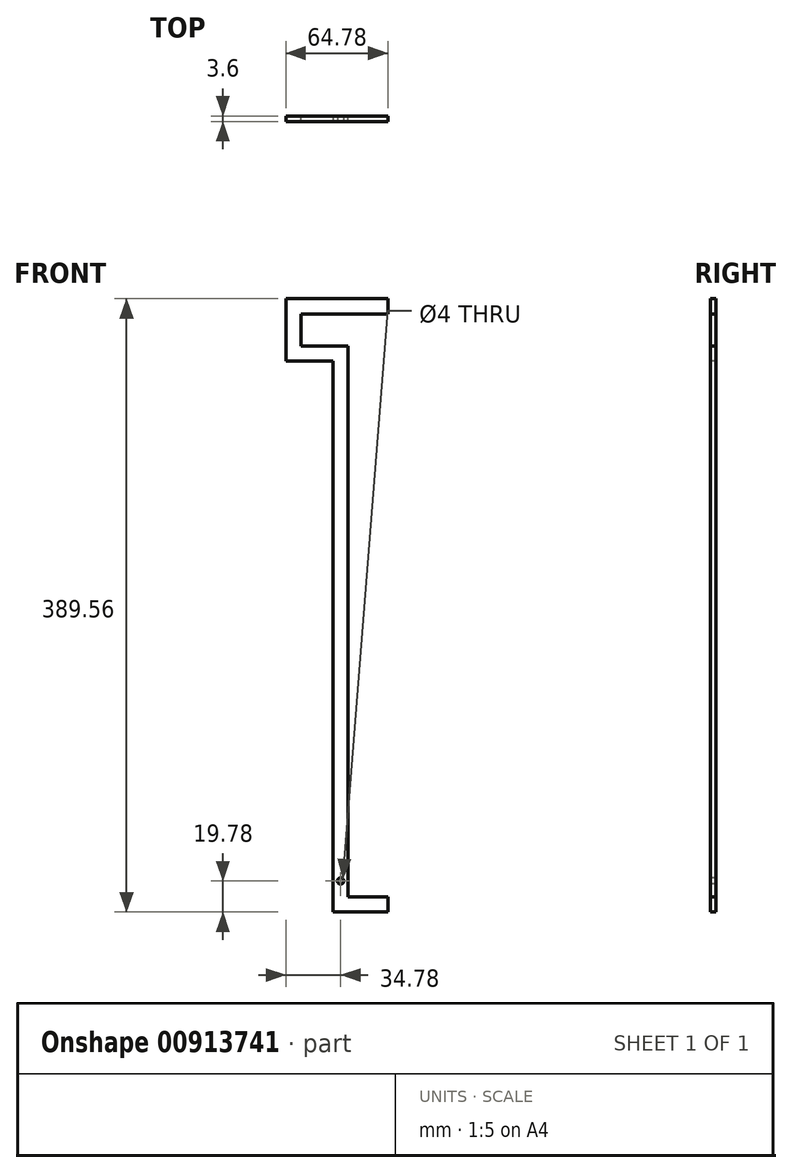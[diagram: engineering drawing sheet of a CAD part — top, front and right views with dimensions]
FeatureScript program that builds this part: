
annotation { "Feature Type Name" : "Feature", "Feature Type Description" : "" }
export const myFeature = defineFeature(function(context is Context, id is Id, definition is map)
    precondition{}
    {
        {
            var Q0;
            Q0=qCreatedBy(makeId("Front.planeOp"),FACE);
            var sketch = newSketch(context, id + "F0", { "sketchPlane" : qUnion([Q0])});
            skLineSegment(sketch, "E0", {"start": v(30, -15) * mm, "end": v(0, -15) * mm});
            skLineSegment(sketch, "E1", {"start": v(0, -15) * mm, "end": v(0, 335) * mm});
            skLineSegment(sketch, "E2", {"start": v(0, 335) * mm, "end": v(-30, 335) * mm});
            skLineSegment(sketch, "E3", {"start": v(-30, 335) * mm, "end": v(-30, 365) * mm});
            skLineSegment(sketch, "E4", {"start": v(-30, 365) * mm, "end": v(30, 365) * mm});
            skPoint(sketch, "E5.startSnap0", {"position": v(0, 0) * mm});
            skSolve(sketch);
        }
        {
            var Q0;
            Q0=qCreatedBy(makeId("Right.planeOp"),FACE);
            var sketch = newSketch(context, id + "F1", { "sketchPlane" : qUnion([Q0])});
            skLineSegment(sketch, "E6.bottom", {"start": v(1.8, -19.78) * mm, "end": v(-1.8, -19.78) * mm});
            skLineSegment(sketch, "E6.top", {"start": v(1.8, -10.22) * mm, "end": v(-1.8, -10.22) * mm});
            skLineSegment(sketch, "E6.left", {"start": v(1.8, -19.78) * mm, "end": v(1.8, -10.22) * mm});
            skLineSegment(sketch, "E6.right", {"start": v(-1.8, -19.78) * mm, "end": v(-1.8, -10.22) * mm});
            skPoint(sketch, "E6.middle", {"position": v(0, -15) * mm});
            skPoint(sketch, "E7.middle", {"position": v(0, -10.22) * mm});
            skSolve(sketch);
        }
        {
            var Q0;
            Q0=makeQuery(id+"F1.imprint","IMPRINT",FACE,{"disambiguationData":[TD([[makeQuery(id+"F1.imprint","IMPRINT",EDGE,{"derivedFrom":sQuery(id+"F1.wireOp",EDGE,"E6.bottom")}),-1.0]])]});
            var Q1;
            Q1=sQuery(id+"F0.wireOp",EDGE,"E0");
            var Q2;
            Q2=sQuery(id+"F0.wireOp",EDGE,"E1");
            var Q3;
            Q3=sQuery(id+"F0.wireOp",EDGE,"E2");
            var Q4;
            Q4=sQuery(id+"F0.wireOp",EDGE,"E3");
            var Q5;
            Q5=sQuery(id+"F0.wireOp",EDGE,"E4");
            sweep(context, id + "F2", {"profiles" : qUnion([Q0]), "path" : qUnion([Q1, Q2, Q3, Q4, Q5])});
        }
        {
            var Q0;
            Q0=makeQuery(id+"F2.opSweep","SWEPT_FACE",FACE,{"disambiguationData":[OSD([sQuery(id+"F0.wireOp",EDGE,"E4"),sQuery(id+"F1.wireOp",EDGE,"E6.right")])]});
            var sketch = newSketch(context, id + "F3", { "sketchPlane" : qUnion([Q0])});
            skCircle(sketch, "E8", {"center": v(0, 0) * mm, "radius": 1.76 * mm});
            skSolve(sketch);
        }
        {
            var Q0;
            Q0=sQuery(id+"F3.wireOp",VERTEX,"E8.center");
            var Q1;
            Q1=makeQuery(id+"F2.opSweep","SWEPT_BODY",BODY,{"disambiguationData":[OSD([sQuery(id+"F0.wireOp",EDGE,"E4"),sQuery(id+"F1.wireOp",EDGE,"E6.bottom"),sQuery(id+"F1.wireOp",EDGE,"E6.top"),sQuery(id+"F1.wireOp",EDGE,"E6.left"),sQuery(id+"F1.wireOp",EDGE,"E6.right")])]});
            hole(context, id + "F4", {"style" : HoleStyle.SIMPLE, "endStyle" : HoleEndStyle.BLIND, "holeDiameter" : 4 * mm, "majorDiameter" : 5 * mm, "holeDepth" : 12 * mm, "isTappedThrough" : true, "tappedDepth" : 12 * mm, "tapClearance" : 3, "locations" : qUnion([Q0]), "scope" : qUnion([Q1])});
        }
    });
